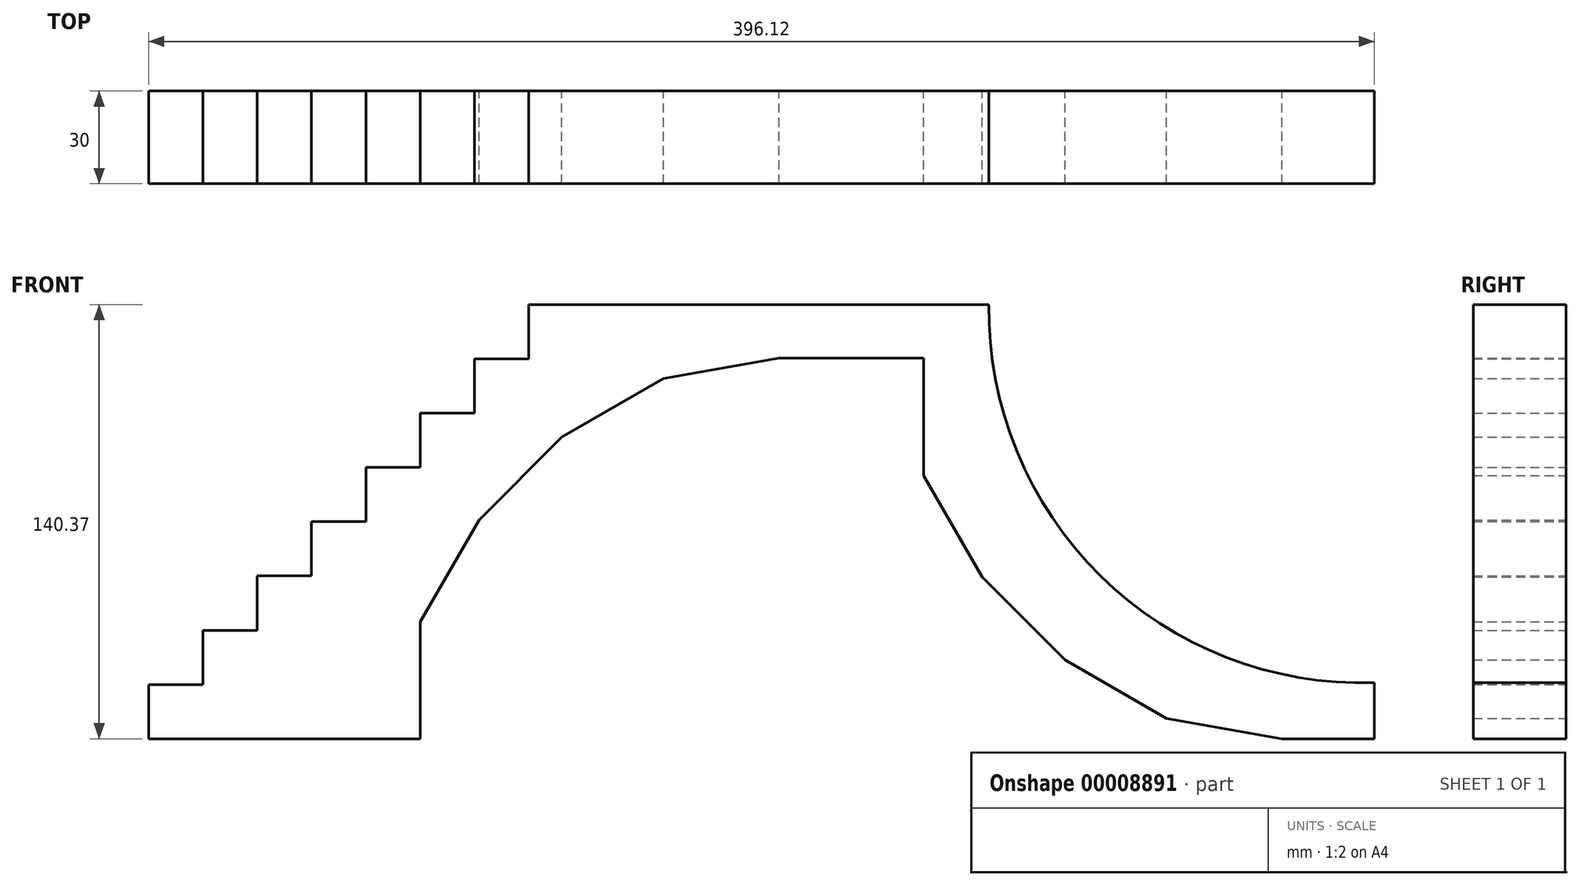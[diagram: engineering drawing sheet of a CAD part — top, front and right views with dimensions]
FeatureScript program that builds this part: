
annotation { "Feature Type Name" : "Feature", "Feature Type Description" : "" }
export const myFeature = defineFeature(function(context is Context, id is Id, definition is map)
    precondition{}
    {
        {
            var Q0;
            Q0=qCreatedBy(makeId("Front.planeOp"),FACE);
            var sketch = newSketch(context, id + "F0", { "sketchPlane" : qUnion([Q0])});
            skLineSegment(sketch, "E0", {"start": v(-183.73, 0) * mm, "end": v(-183.73, 37.89) * mm});
            skLineSegment(sketch, "E1", {"start": v(-138, 97.5) * mm, "end": v(-105.19, 116.43) * mm});
            skLineSegment(sketch, "E2", {"start": v(-105.19, 116.43) * mm, "end": v(-67.87, 123.01) * mm});
            skLineSegment(sketch, "E3", {"start": v(-67.87, 123.01) * mm, "end": v(-21.1, 123.01) * mm});
            skLineSegment(sketch, "E4", {"start": v(-2.15, 52.31) * mm, "end": v(24.64, 25.52) * mm});
            skLineSegment(sketch, "E5", {"start": v(24.64, 25.52) * mm, "end": v(57.46, 6.58) * mm});
            skLineSegment(sketch, "E6", {"start": v(57.46, 6.58) * mm, "end": v(94.77, 0) * mm});
            skLineSegment(sketch, "E7", {"start": v(94.77, 0) * mm, "end": v(124.56, 0) * mm});
            skLineSegment(sketch, "E8", {"start": v(-21.1, 123.01) * mm, "end": v(-21.1, 85.13) * mm});
            skLineSegment(sketch, "E9", {"start": v(-21.1, 85.13) * mm, "end": v(-2.15, 52.31) * mm});
            skLineSegment(sketch, "E10", {"start": v(-183.73, 37.89) * mm, "end": v(-164.79, 70.7) * mm});
            skLineSegment(sketch, "E11", {"start": v(-164.79, 70.7) * mm, "end": v(-138, 97.5) * mm});
            skLineSegment(sketch, "E12", {"start": v(-183.73, 0) * mm, "end": v(-271.56, 0) * mm});
            skLineSegment(sketch, "E13", {"start": v(-271.56, 0) * mm, "end": v(-271.56, 17.55) * mm});
            skLineSegment(sketch, "E14", {"start": v(-271.56, 17.55) * mm, "end": v(-254, 17.55) * mm});
            skLineSegment(sketch, "E15", {"start": v(-254, 17.55) * mm, "end": v(-254, 35.1) * mm});
            skLineSegment(sketch, "E16", {"start": v(-254, 35.1) * mm, "end": v(-236.46, 35.1) * mm});
            skLineSegment(sketch, "E17", {"start": v(-236.46, 35.1) * mm, "end": v(-236.46, 52.64) * mm});
            skLineSegment(sketch, "E18", {"start": v(-236.46, 52.64) * mm, "end": v(-218.92, 52.64) * mm});
            skLineSegment(sketch, "E19", {"start": v(-218.92, 52.64) * mm, "end": v(-218.92, 70.19) * mm});
            skLineSegment(sketch, "E20", {"start": v(-218.92, 70.19) * mm, "end": v(-201.37, 70.19) * mm});
            skLineSegment(sketch, "E21", {"start": v(-201.37, 70.19) * mm, "end": v(-201.37, 87.73) * mm});
            skLineSegment(sketch, "E22", {"start": v(-201.37, 87.73) * mm, "end": v(-183.82, 87.73) * mm});
            skLineSegment(sketch, "E23", {"start": v(-183.82, 87.73) * mm, "end": v(-183.82, 105.28) * mm});
            skLineSegment(sketch, "E24", {"start": v(-183.82, 105.28) * mm, "end": v(-166.28, 105.28) * mm});
            skLineSegment(sketch, "E25", {"start": v(-166.28, 105.28) * mm, "end": v(-166.28, 122.83) * mm});
            skLineSegment(sketch, "E26", {"start": v(-166.28, 122.83) * mm, "end": v(-148.73, 122.83) * mm});
            skLineSegment(sketch, "E27", {"start": v(-148.73, 122.83) * mm, "end": v(-148.73, 140.37) * mm});
            skLineSegment(sketch, "E28", {"start": v(-148.73, 140.37) * mm, "end": v(0, 140.37) * mm});
            skArc(sketch, "E29", {"start": v(0, 140.37) * mm, "mid": v(36.14, 52.62) * mm, "end": v(124.56, 18.13) * mm});
            skLineSegment(sketch, "E30", {"start": v(124.56, 18.13) * mm, "end": v(124.56, 0) * mm});
            skSolve(sketch);
        }
        {
            var Q0;
            Q0 = qSketchRegion(id + "F0", true);
            extrude(context, id + "F1", {"entities" : qUnion([Q0]), "depth" : 30 * mm});
        }
    });
